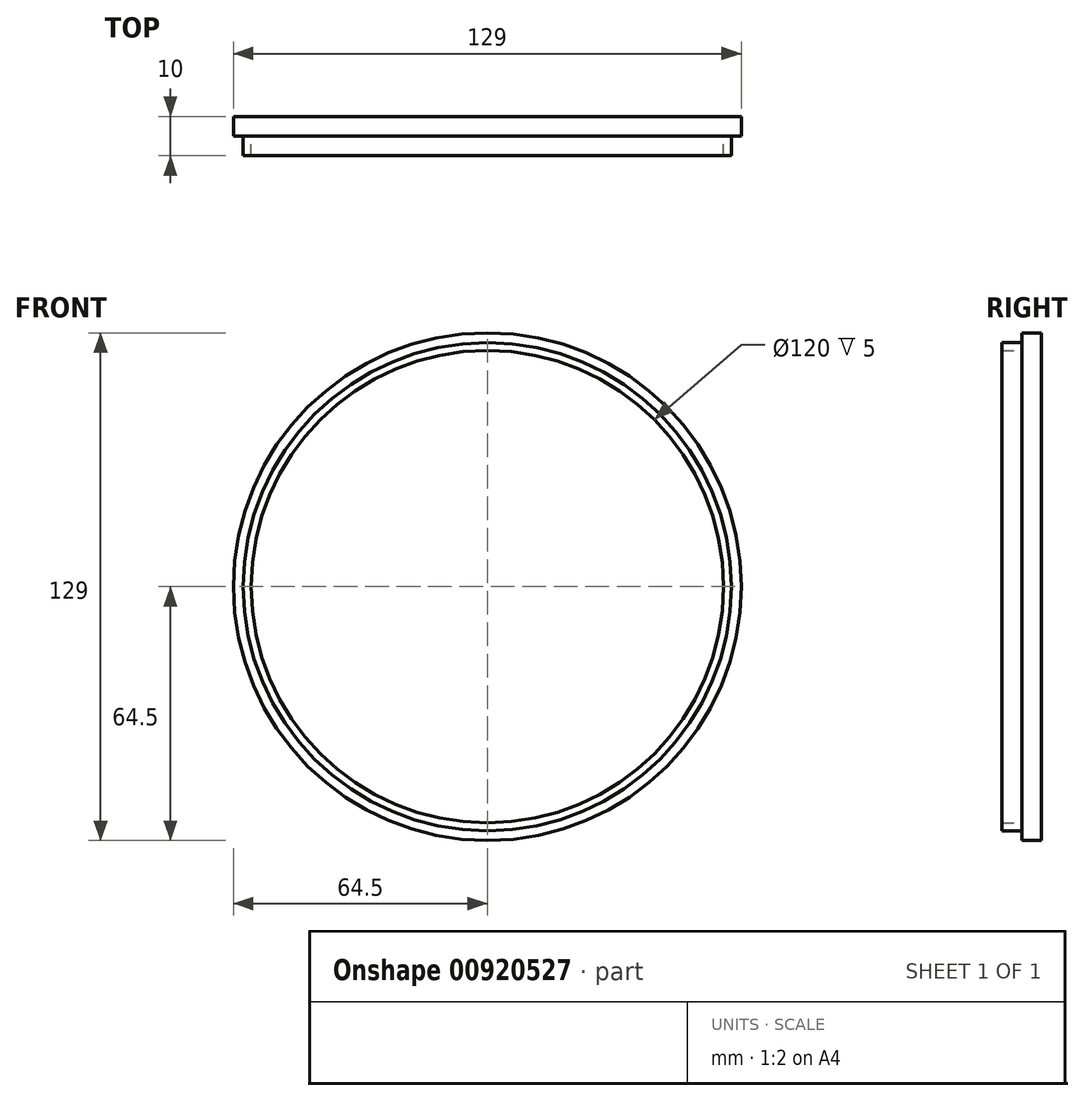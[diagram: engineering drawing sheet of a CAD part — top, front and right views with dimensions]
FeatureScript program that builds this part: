
annotation { "Feature Type Name" : "Feature", "Feature Type Description" : "" }
export const myFeature = defineFeature(function(context is Context, id is Id, definition is map)
    precondition{}
    {
        {
            var Q0;
            Q0=qCreatedBy(makeId("Front.planeOp"),FACE);
            var sketch = newSketch(context, id + "F0", { "sketchPlane" : qUnion([Q0])});
            skCircle(sketch, "E0", {"center": v(0, 0) * mm, "radius": 62 * mm});
            skCircle(sketch, "E1", {"center": v(0, 0) * mm, "radius": 60 * mm});
            skCircle(sketch, "E2", {"center": v(0, 0) * mm, "radius": 64.5 * mm});
            skSolve(sketch);
        }
        {
            var Q0;
            Q0=makeQuery(id+"F0.imprint","IMPRINT",FACE,{"disambiguationData":[TD([[makeQuery(id+"F0.imprint","IMPRINT",EDGE,{"derivedFrom":sQuery(id+"F0.wireOp",EDGE,"E1")}),1.0]])]});
            var Q1;
            Q1=makeQuery(id+"F0.imprint","IMPRINT",FACE,{"disambiguationData":[TD([[makeQuery(id+"F0.imprint","IMPRINT",EDGE,{"derivedFrom":sQuery(id+"F0.wireOp",EDGE,"E0")}),-1.0]])]});
            var Q2;
            Q2=makeQuery(id+"F0.imprint","IMPRINT",FACE,{"disambiguationData":[TD([[makeQuery(id+"F0.imprint","IMPRINT",EDGE,{"derivedFrom":sQuery(id+"F0.wireOp",EDGE,"E0")}),1.0]])]});
            extrude(context, id + "F1", {"entities" : qUnion([Q0, Q1, Q2]), "depth" : 5 * mm, "offsetDistance" : 25 * mm});
        }
        {
            var Q0;
            Q0=makeQuery(id+"F0.imprint","IMPRINT",FACE,{"disambiguationData":[TD([[makeQuery(id+"F0.imprint","IMPRINT",EDGE,{"derivedFrom":sQuery(id+"F0.wireOp",EDGE,"E0")}),1.0]])]});
            extrude(context, id + "F2", {"entities" : qUnion([Q0]), "operationType" : NewBodyOperationType.ADD, "depth" : 10 * mm, "offsetDistance" : 25 * mm});
        }
    });
